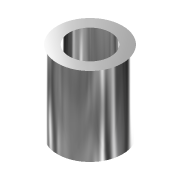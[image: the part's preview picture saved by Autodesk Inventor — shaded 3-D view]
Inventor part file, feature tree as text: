
AUTODESK INVENTOR PART (.ipt)
format: ipt  version: 2012 (Build 160160000, 160)  size: 80,896 bytes
history: native  units: mm
features: extrude x1, sketch x1
ambient origin geometry x8: Origin, YZ Plane, XZ Plane, XY Plane, X Axis, Y Axis, Z Axis, Center Point
bodies: Solid1 (feature_tree)
feature tree (2):
  extrude  "Extrusion1"  Depth=5.1mm
  sketch  "Sketch1"  dims[d0=8.0mm d1=5.1mm d2=9.7mm d3=0.0mm]
